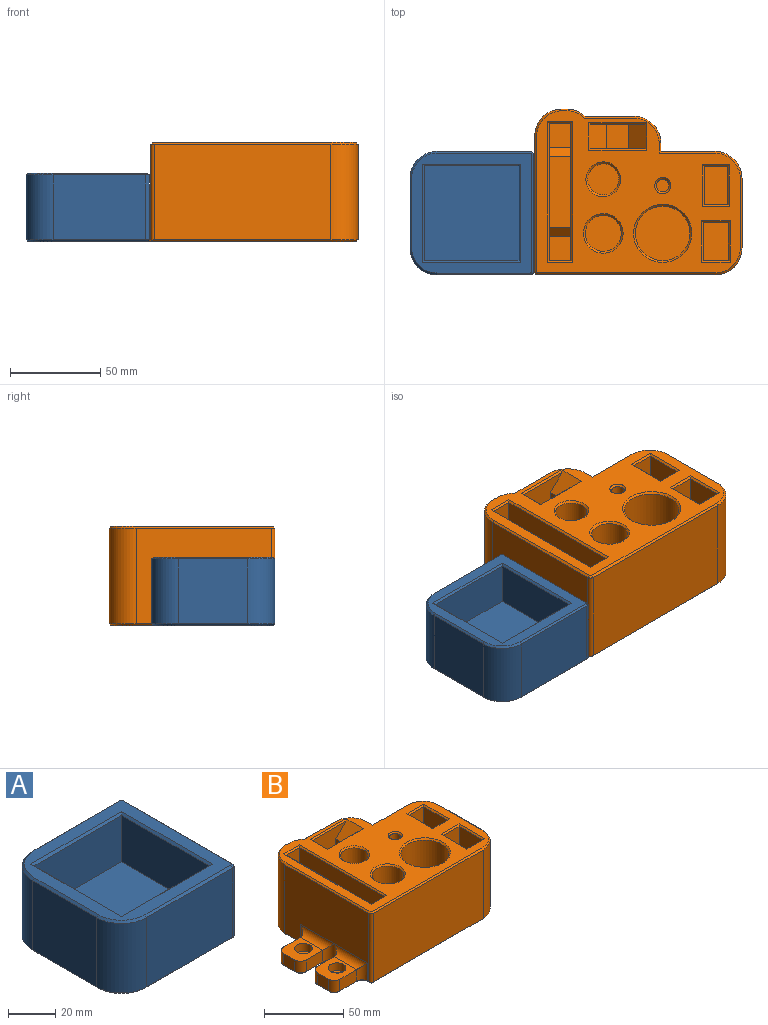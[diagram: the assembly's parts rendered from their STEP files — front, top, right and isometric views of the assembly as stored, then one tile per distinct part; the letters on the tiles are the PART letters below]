
ASSEMBLY  parts=2 mates=1
PART A: 66 faces, bbox 68.5x68.5x38 mm
  f0: plane 64.5x36mm, normal (1,0,0), area 1482mm2, adj f26,f27,f29,f30,f35,f36,f38,f52
  f1: plane 51.5x36mm, normal (0,1,0), area 1854mm2, adj f11,f17,f36,f58
  f2: plane 38.5x36mm, normal (-1,0,0), area 1386mm2, adj f11,f12,f15,f61
  f3: plane 51.5x36mm, normal (0,-1,0), area 1854mm2, adj f12,f13,f35,f57
  f4: plane 52.5x24mm, normal (0,1,0), area 1260mm2, adj f5,f7,f10,f64
  f5: plane 52.5x24mm, normal (1,0,0), area 1260mm2, adj f4,f6,f10,f62
  f6: plane 52.5x24mm, normal (0,-1,0), area 1260mm2, adj f5,f7,f10,f63
  f7: plane 52.5x24mm, normal (-1,0,0), area 1260mm2, adj f4,f6,f10,f65
  f8: plane 66.5x66.5mm, normal (0,0,1), area 1367.4mm2, adj f54,f55,f56,f57,f58,f59,f60,f61
  f9: plane 66.5x66.5mm, normal (0,0,-1), area 3254.9mm2, adj f13,f14,f15,f16,f17,f37,f38,f39
  f10: plane 52.5x52.5mm, normal (0,0,1), area 2756.2mm2, adj f4,f5,f6,f7
  f11: cylinder r=15mm len=36mm, axis (0,0,-1), area 848.2mm2, adj f1,f2,f16,f60
  f12: cylinder r=15mm len=36mm, axis (0,0,1), area 848.2mm2, adj f2,f3,f14,f59
  f13: plane 51.5x1mm, normal (0,-0.71,-0.71), area 72.8mm2, adj f3,f9,f14,f37
  f14: cone r=14mm half-angle=45deg, axis (0,0,1), area 32.2mm2, adj f9,f12,f13,f15
  f15: plane 38.5x1mm, normal (-0.71,0,-0.71), area 54.4mm2, adj f2,f9,f14,f16
  f16: cone r=14mm half-angle=45deg, axis (0,0,1), area 32.2mm2, adj f9,f11,f15,f17
  f17: plane 51.5x1mm, normal (0,0.71,-0.71), area 72.8mm2, adj f1,f9,f16,f53
  f18: plane 15x9mm, normal (0,-1,0), area 135mm2, adj f19,f29,f31,f50
  f19: plane 20x20mm, normal (0,0,-1), area 389.3mm2, adj f18,f20,f21,f30,f31,f32
  f20: plane 15x9mm, normal (0,1,0), area 135mm2, adj f19,f28,f32,f46
  f21: plane 10x9mm, normal (1,0,0), area 90mm2, adj f19,f31,f32,f48
  f22: plane 15x9mm, normal (0,-1,0), area 135mm2, adj f23,f28,f33,f44
  f23: plane 20x20mm, normal (0,0,-1), area 389.3mm2, adj f22,f24,f25,f27,f33,f34
  f24: plane 15x9mm, normal (0,1,0), area 135mm2, adj f23,f26,f34,f40
  f25: plane 10x9mm, normal (1,0,0), area 90mm2, adj f23,f33,f34,f42
  f26: cylinder r=5mm len=14mm, axis (0,0,-1), area 85mm2, adj f0,f24,f27,f39
  f27: cylinder r=5mm len=30mm, axis (0,-1,0), area 185.6mm2, adj f0,f23,f26,f28
  f28: cylinder r=5mm len=14mm, axis (0,0,1), area 169.9mm2, adj f20,f22,f27,f30,f45
  f29: cylinder r=5mm len=14mm, axis (0,0,1), area 85mm2, adj f0,f18,f30,f51
  f30: cylinder r=5mm len=30mm, axis (0,-1,0), area 185.6mm2, adj f0,f19,f28,f29
  f31: cylinder r=5mm len=9mm, axis (0,0,1), area 70.7mm2, adj f18,f19,f21,f49
  f32: cylinder r=5mm len=9mm, axis (0,0,-1), area 70.7mm2, adj f19,f20,f21,f47
  f33: cylinder r=5mm len=9mm, axis (0,0,1), area 70.7mm2, adj f22,f23,f25,f43
  f34: cylinder r=5mm len=9mm, axis (0,0,-1), area 70.7mm2, adj f23,f24,f25,f41
  f35: cylinder r=2mm len=36mm, axis (0,0,-1), area 113.1mm2, adj f0,f3,f37,f55
  f36: cylinder r=2mm len=36mm, axis (0,0,1), area 113.1mm2, adj f0,f1,f53,f56
  f37: cone r=1mm half-angle=45deg, axis (0,0,1), area 3.3mm2, adj f9,f13,f35,f38
  f38: plane 1x1mm, normal (0.71,0,-0.71), area 1.4mm2, adj f0,f9,f37,f39
  f39: cone r=4mm half-angle=45deg, axis (0,0,1), area 10mm2, adj f9,f26,f38,f40
  f40: plane 15x1mm, normal (0,0.71,-0.71), area 21.2mm2, adj f9,f24,f39,f41
  f41: cone r=6mm half-angle=45deg, axis (0,0,-1), area 12.2mm2, adj f9,f34,f40,f42
  f42: plane 10x1mm, normal (0.71,0,-0.71), area 14.1mm2, adj f9,f25,f41,f43
  f43: cone r=6mm half-angle=45deg, axis (0,0,-1), area 12.2mm2, adj f9,f33,f42,f44
  f44: plane 15x1mm, normal (0,-0.71,-0.71), area 21.2mm2, adj f9,f22,f43,f45
  f45: cone r=4mm half-angle=45deg, axis (0,0,1), area 20mm2, adj f9,f28,f44,f46
  f46: plane 15x1mm, normal (0,0.71,-0.71), area 21.2mm2, adj f9,f20,f45,f47
  f47: cone r=6mm half-angle=45deg, axis (0,0,-1), area 12.2mm2, adj f9,f32,f46,f48
  f48: plane 10x1mm, normal (0.71,0,-0.71), area 14.1mm2, adj f9,f21,f47,f49
  f49: cone r=6mm half-angle=45deg, axis (0,0,-1), area 12.2mm2, adj f9,f31,f48,f50
  f50: plane 15x1mm, normal (0,-0.71,-0.71), area 21.2mm2, adj f9,f18,f49,f51
  f51: cone r=4mm half-angle=45deg, axis (0,0,1), area 10mm2, adj f9,f29,f50,f52
  f52: plane 3.5x1mm, normal (0.71,0,-0.71), area 4.9mm2, adj f0,f9,f51,f53
  f53: cone r=1mm half-angle=45deg, axis (0,0,1), area 3.3mm2, adj f9,f17,f36,f52
  f54: plane 64.5x1mm, normal (0.71,0,0.71), area 91.2mm2, adj f0,f8,f55,f56
  f55: cone r=1mm half-angle=45deg, axis (0,0,-1), area 3.3mm2, adj f8,f35,f54,f57
  f56: cone r=1mm half-angle=45deg, axis (0,0,-1), area 3.3mm2, adj f8,f36,f54,f58
  f57: plane 51.5x1mm, normal (0,-0.71,0.71), area 72.8mm2, adj f3,f8,f55,f59
  f58: plane 51.5x1mm, normal (0,0.71,0.71), area 72.8mm2, adj f1,f8,f56,f60
  f59: cone r=14mm half-angle=45deg, axis (0,0,-1), area 32.2mm2, adj f8,f12,f57,f61
  f60: cone r=14mm half-angle=45deg, axis (0,0,-1), area 32.2mm2, adj f8,f11,f58,f61
  f61: plane 38.5x1mm, normal (-0.71,0,0.71), area 54.4mm2, adj f2,f8,f59,f60
  f62: plane 54.5x1mm, normal (0.71,0,0.71), area 75.7mm2, adj f5,f8,f63,f64
  f63: plane 54.5x1mm, normal (0,-0.71,0.71), area 75.7mm2, adj f6,f8,f62,f65
  f64: plane 54.5x1mm, normal (0,0.71,0.71), area 75.7mm2, adj f4,f8,f62,f65
  f65: plane 54.5x1mm, normal (-0.71,0,0.71), area 75.7mm2, adj f7,f8,f63,f64
PART B: 131 faces, bbox 140x92x55 mm
  f0: plane 49x30mm, normal (0,-1,0), area 669mm2, adj f31,f39,f40,f41,f42,f126
  f1: plane 76x49mm, normal (-1,0,0), area 2769mm2, adj f9,f11,f32,f33,f34,f35,f36,f37
  f2: plane 75x53mm, normal (-1,0,0), area 3135mm2, adj f59,f60,f62,f63,f72,f74,f98,f99
  f3: plane 98x53mm, normal (0,-1,0), area 5194mm2, adj f68,f96,f99,f103
  f4: plane 53x38.5mm, normal (1,0,0), area 2040.5mm2, adj f68,f69,f92,f100
  f5: plane 53x30mm, normal (0,1,0), area 1590mm2, adj f6,f69,f88,f104
  f6: plane 53x4.5mm, normal (1,0,0), area 238.5mm2, adj f5,f70,f86,f106
  f7: plane 53x27mm, normal (0,1,0), area 1431mm2, adj f70,f71,f82,f110
  f8: plane 49x30mm, normal (0,1,0), area 669mm2, adj f31,f39,f40,f41,f42,f127
  f9: plane 49x12mm, normal (0,1,0), area 588mm2, adj f1,f10,f33,f125
  f10: plane 76x49mm, normal (1,0,0), area 2769mm2, adj f9,f11,f32,f33,f34,f35,f36,f37
  f11: plane 49x12mm, normal (0,-1,0), area 588mm2, adj f1,f10,f32,f122
  f12: plane 45x14mm, normal (0,1,0), area 630mm2, adj f13,f18,f43,f116
  f13: plane 45x21mm, normal (1,0,0), area 945mm2, adj f12,f14,f43,f114
  f14: plane 45x14mm, normal (0,-1,0), area 630mm2, adj f13,f18,f43,f113
  f15: plane 49x13mm, normal (0,-1,0), area 637mm2, adj f16,f19,f30,f120
  f16: plane 49x21mm, normal (-1,0,0), area 1029mm2, adj f15,f17,f30,f118
  f17: plane 49x13mm, normal (0,1,0), area 637mm2, adj f16,f19,f30,f119
  f18: plane 45x21mm, normal (-1,0,0), area 945mm2, adj f12,f14,f43,f115
  f19: plane 49x21mm, normal (1,0,0), area 1029mm2, adj f15,f17,f30,f121
  f20: cylinder r=8.65mm len=49mm, axis (0,0,-1), area 2663.1mm2, adj f27,f128
  f21: cylinder r=10mm len=49mm, axis (0,0,-1), area 3078.8mm2, adj f28,f117
  f22: cylinder r=3.5mm len=49mm, axis (0,0,-1), area 1077.6mm2, adj f29,f129
  f23: cylinder r=15.15mm len=44mm, axis (0,0,-1), area 4188.4mm2, adj f44,f130
  f24: plane 53x2.8mm, normal (0,1,0), area 148.5mm2, adj f71,f72,f78,f111
  f25: plane 113x90mm, normal (0,0,1), area 4909.5mm2, adj f41,f42,f100,f101,f102,f103,f104,f105
  f26: plane 138x90mm, normal (0,0,-1), area 9615.2mm2, adj f53,f56,f73,f74,f75,f76,f77,f78
  f27: plane 17.3x17.3mm, normal (0,0,1), area 235.1mm2, adj f20
  f28: plane 20x20mm, normal (0,0,1), area 314.2mm2, adj f21
  f29: plane 7x7mm, normal (0,0,1), area 38.5mm2, adj f22
  f30: plane 21x13mm, normal (0,0,1), area 273mm2, adj f15,f16,f17,f19
  f31: plane 13.5x12mm, normal (0,0,1), area 162mm2, adj f0,f8,f39,f40
  f32: plane 13.5x12mm, normal (0,0,1), area 162mm2, adj f1,f10,f11,f36
  f33: plane 13.5x12mm, normal (0,0,1), area 162mm2, adj f1,f9,f10,f35
  f34: plane 39x12mm, normal (0,0,1), area 468mm2, adj f1,f10,f37,f38
  f35: plane 15x12mm, normal (0,-1,0), area 180mm2, adj f1,f10,f33,f37
  f36: plane 15x12mm, normal (0,1,0), area 180mm2, adj f1,f10,f32,f38
  f37: plane 12x5mm, normal (0,-0.71,0.71), area 84.9mm2, adj f1,f10,f34,f35
  f38: plane 12x5mm, normal (0,0.71,0.71), area 84.9mm2, adj f1,f10,f34,f36
  f39: plane 40x13.5mm, normal (1,0,0), area 540mm2, adj f0,f8,f31,f42
  f40: plane 40x13.5mm, normal (-1,0,0), area 540mm2, adj f0,f8,f31,f41
  f41: plane 15.5x10mm, normal (-0.71,0,0.71), area 192.3mm2, adj f0,f8,f25,f40,f126,f127
  f42: plane 15.5x10mm, normal (0.71,0,0.71), area 192.3mm2, adj f0,f8,f25,f39,f126,f127
  f43: plane 21x14mm, normal (0,0,1), area 294mm2, adj f12,f13,f14,f18
  f44: plane 30.3x30.3mm, normal (0,0,1), area 721.1mm2, adj f23
  f45: plane 15x9mm, normal (0,-1,0), area 135mm2, adj f48,f63,f65,f95
  f46: plane 15x9mm, normal (0,1,0), area 135mm2, adj f48,f61,f64,f87
  f47: plane 10x9mm, normal (-1,0,0), area 90mm2, adj f48,f64,f65,f91
  f48: plane 20x20mm, normal (0,0,1), area 289.9mm2, adj f45,f46,f47,f58,f62,f64,f65
  f49: plane 15x9mm, normal (0,-1,0), area 135mm2, adj f52,f61,f66,f83
  f50: plane 15x9mm, normal (0,1,0), area 135mm2, adj f52,f59,f67,f75
  f51: plane 10x9mm, normal (-1,0,0), area 90mm2, adj f52,f66,f67,f79
  f52: plane 20x20mm, normal (0,0,1), area 289.9mm2, adj f49,f50,f51,f55,f60,f66,f67
  f53: cylinder r=3.3mm len=6.6mm, axis (0,0,1), area 82.9mm2, adj f26,f54
  f54: plane 11.25x11.25mm, normal (0,0,1), area 65.2mm2, adj f53,f55
  f55: cylinder r=5.62mm len=11.25mm, axis (0,0,1), area 212.1mm2, adj f52,f54
  f56: cylinder r=3.3mm len=6.6mm, axis (0,0,1), area 82.9mm2, adj f26,f57
  f57: plane 11.25x11.25mm, normal (0,0,1), area 65.2mm2, adj f56,f58
  f58: cylinder r=5.62mm len=11.25mm, axis (0,0,1), area 212.1mm2, adj f48,f57
  f59: cylinder r=5mm len=14mm, axis (0,0,-1), area 85mm2, adj f2,f50,f60,f73
  f60: cylinder r=5mm len=30mm, axis (0,-1,0), area 185.6mm2, adj f2,f52,f59,f61
  f61: cylinder r=5mm len=14mm, axis (0,0,1), area 169.9mm2, adj f46,f49,f60,f62,f85
  f62: cylinder r=5mm len=30mm, axis (0,-1,0), area 185.6mm2, adj f2,f48,f61,f63
  f63: cylinder r=5mm len=14mm, axis (0,0,1), area 85mm2, adj f2,f45,f62,f97
  f64: cylinder r=5mm len=9mm, axis (0,0,1), area 70.7mm2, adj f46,f47,f48,f89
  f65: cylinder r=5mm len=9mm, axis (0,0,-1), area 70.7mm2, adj f45,f47,f48,f93
  f66: cylinder r=5mm len=9mm, axis (0,0,-1), area 70.7mm2, adj f49,f51,f52,f81
  f67: cylinder r=5mm len=9mm, axis (0,0,1), area 70.7mm2, adj f50,f51,f52,f77
  f68: cylinder r=15mm len=53mm, axis (0,0,1), area 1248.8mm2, adj f3,f4,f94,f101
  f69: cylinder r=15mm len=53mm, axis (0,0,1), area 1248.8mm2, adj f4,f5,f90,f102
  f70: cylinder r=15mm len=53mm, axis (0,0,-1), area 1248.8mm2, adj f6,f7,f84,f108
  f71: cylinder r=15mm len=53mm, axis (0,0,1), area 594.3mm2, adj f7,f24,f80,f112
  f72: cylinder r=15mm len=53mm, axis (0,0,-1), area 1248.8mm2, adj f2,f24,f76,f109
  f73: cone r=6mm half-angle=45deg, axis (0,0,-1), area 12.2mm2, adj f26,f59,f74,f75
  f74: plane 14x1mm, normal (-0.71,0,-0.71), area 19.8mm2, adj f2,f26,f73,f76
  f75: plane 15x1mm, normal (0,0.71,-0.71), area 21.2mm2, adj f26,f50,f73,f77
  f76: cone r=14mm half-angle=45deg, axis (0,0,1), area 32.2mm2, adj f26,f72,f74,f78
  f77: cone r=4mm half-angle=45deg, axis (0,0,1), area 10mm2, adj f26,f67,f75,f79
  f78: plane 2.8x1mm, normal (0,0.71,-0.71), area 4mm2, adj f24,f26,f76,f80
  f79: plane 10x1mm, normal (-0.71,0,-0.71), area 14.1mm2, adj f26,f51,f77,f81
  f80: cone r=14mm half-angle=45deg, axis (0,0,1), area 15.6mm2, adj f26,f71,f78,f82
  f81: cone r=4mm half-angle=45deg, axis (0,0,1), area 10mm2, adj f26,f66,f79,f83
  f82: plane 27.41x1.01mm, normal (0,0.71,-0.71), area 38.5mm2, adj f7,f26,f80,f84
  f83: plane 15x1mm, normal (0,-0.71,-0.71), area 21.2mm2, adj f26,f49,f81,f85
  f84: cone r=14mm half-angle=45deg, axis (0,0,1), area 32.2mm2, adj f26,f70,f82,f86
  f85: cone r=6mm half-angle=45deg, axis (0,0,-1), area 24.4mm2, adj f26,f61,f83,f87
  f86: plane 5.5x1mm, normal (0.71,0,-0.71), area 7.1mm2, adj f6,f26,f84,f88
  f87: plane 15x1mm, normal (0,0.71,-0.71), area 21.2mm2, adj f26,f46,f85,f89
  f88: plane 31x1mm, normal (0,0.71,-0.71), area 43.1mm2, adj f5,f26,f86,f90
  f89: cone r=4mm half-angle=45deg, axis (0,0,1), area 10mm2, adj f26,f64,f87,f91
  f90: cone r=14mm half-angle=45deg, axis (0,0,1), area 32.2mm2, adj f26,f69,f88,f92
  f91: plane 10x1mm, normal (-0.71,0,-0.71), area 14.1mm2, adj f26,f47,f89,f93
  f92: plane 38.5x1mm, normal (0.71,0,-0.71), area 54.4mm2, adj f4,f26,f90,f94
  f93: cone r=4mm half-angle=45deg, axis (0,0,1), area 10mm2, adj f26,f65,f91,f95
  f94: cone r=14mm half-angle=45deg, axis (0,0,1), area 32.2mm2, adj f26,f68,f92,f96
  f95: plane 15x1mm, normal (0,-0.71,-0.71), area 21.2mm2, adj f26,f45,f93,f97
  f96: plane 99.41x1mm, normal (0,-0.71,-0.71), area 140.1mm2, adj f3,f26,f94,f98,f99
  f97: cone r=6mm half-angle=45deg, axis (0,0,-1), area 12.2mm2, adj f26,f63,f95,f98
  f98: plane 2.41x1mm, normal (-0.71,0,-0.71), area 2.9mm2, adj f2,f26,f96,f97,f99
  f99: cylinder r=2mm len=53.59mm, axis (0,0,1), area 167.1mm2, adj f2,f3,f96,f98,f105
  f100: plane 38.5x1mm, normal (0.71,0,0.71), area 54.4mm2, adj f4,f25,f101,f102
  f101: cone r=14mm half-angle=45deg, axis (0,0,-1), area 32.2mm2, adj f25,f68,f100,f103
  f102: cone r=14mm half-angle=45deg, axis (0,0,-1), area 32.2mm2, adj f25,f69,f100,f104
  f103: plane 98x1mm, normal (0,-0.71,0.71), area 138.6mm2, adj f3,f25,f101,f105
  f104: plane 31x1mm, normal (0,0.71,0.71), area 43.1mm2, adj f5,f25,f102,f106
  f105: cone r=1mm half-angle=45deg, axis (0,0,-1), area 3.3mm2, adj f25,f99,f103,f107
  f106: plane 5.5x1mm, normal (0.71,0,0.71), area 7.1mm2, adj f6,f25,f104,f108
  f107: plane 75x1mm, normal (-0.71,0,0.71), area 106.1mm2, adj f2,f25,f105,f109
  f108: cone r=14mm half-angle=45deg, axis (0,0,-1), area 32.2mm2, adj f25,f70,f106,f110
  f109: cone r=14mm half-angle=45deg, axis (0,0,-1), area 32.2mm2, adj f25,f72,f107,f111
  f110: plane 27.41x1.01mm, normal (0,0.71,0.71), area 38.5mm2, adj f7,f25,f108,f112
  f111: plane 2.8x1mm, normal (0,0.71,0.71), area 4mm2, adj f24,f25,f109,f112
  f112: cone r=14mm half-angle=45deg, axis (0,0,-1), area 15.6mm2, adj f25,f71,f110,f111
  f113: plane 16x1mm, normal (0,-0.71,0.71), area 21.2mm2, adj f14,f25,f114,f115
  f114: plane 23x1mm, normal (0.71,0,0.71), area 31.1mm2, adj f13,f25,f113,f116
  f115: plane 23x1mm, normal (-0.71,0,0.71), area 31.1mm2, adj f18,f25,f113,f116
  f116: plane 16x1mm, normal (0,0.71,0.71), area 21.2mm2, adj f12,f25,f114,f115
  f117: cone r=10mm half-angle=45deg, axis (0,0,1), area 93.3mm2, adj f21,f25
  f118: plane 23x1mm, normal (-0.71,0,0.71), area 31.1mm2, adj f16,f25,f119,f120
  f119: plane 15x1mm, normal (0,0.71,0.71), area 19.8mm2, adj f17,f25,f118,f121
  f120: plane 15x1mm, normal (0,-0.71,0.71), area 19.8mm2, adj f15,f25,f118,f121
  f121: plane 23x1mm, normal (0.71,0,0.71), area 31.1mm2, adj f19,f25,f119,f120
  f122: plane 14x1mm, normal (0,-0.71,0.71), area 18.4mm2, adj f11,f25,f123,f124
  f123: plane 78x1mm, normal (0.71,0,0.71), area 108.9mm2, adj f10,f25,f122,f125
  f124: plane 78x1mm, normal (-0.71,0,0.71), area 108.9mm2, adj f1,f25,f122,f125
  f125: plane 14x1mm, normal (0,0.71,0.71), area 18.4mm2, adj f9,f25,f123,f124
  f126: plane 32x1mm, normal (0,-0.71,0.71), area 43.8mm2, adj f0,f25,f41,f42
  f127: plane 32x1mm, normal (0,0.71,0.71), area 43.8mm2, adj f8,f25,f41,f42
  f128: cone r=8.65mm half-angle=45deg, axis (0,0,1), area 81.3mm2, adj f20,f25
  f129: cone r=3.5mm half-angle=45deg, axis (0,0,1), area 35.5mm2, adj f22,f25
  f130: cone r=15.15mm half-angle=45deg, axis (0,0,1), area 139.1mm2, adj f23,f25
PLACE A t=(-598.86,35.36,-52.46)mm
PLACE B t=(-404.58,35.36,-52.46)mm
MATE fastened A.f23 <-> B.f48  axis (0,0,-1) through (37.29,75.86,-42.46)mm
